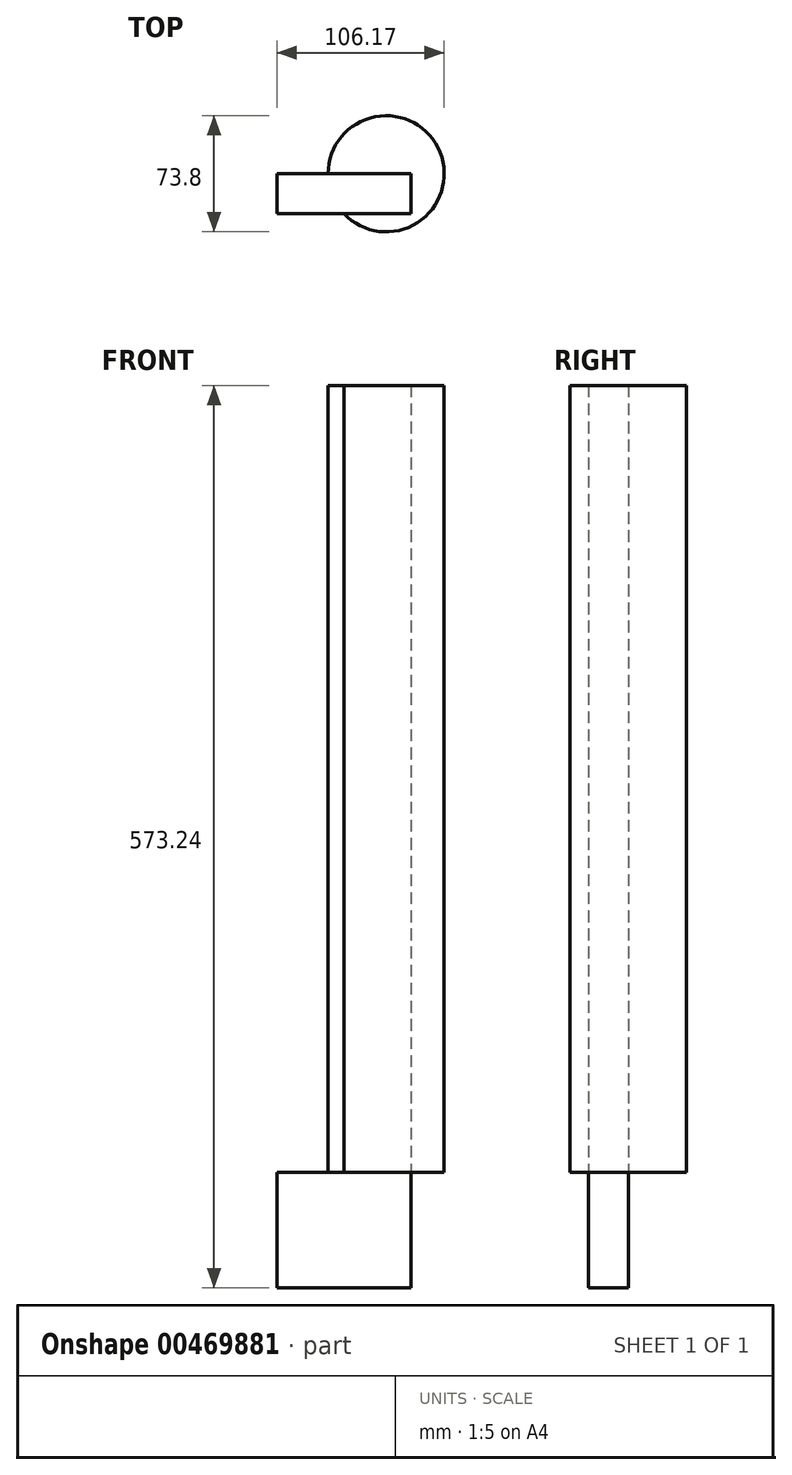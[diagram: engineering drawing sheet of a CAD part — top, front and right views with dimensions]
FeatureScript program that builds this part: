
annotation { "Feature Type Name" : "Feature", "Feature Type Description" : "" }
export const myFeature = defineFeature(function(context is Context, id is Id, definition is map)
    precondition{}
    {
        {
            var Q0;
            Q0=qCreatedBy(makeId("Front.planeOp"),FACE);
            var sketch = newSketch(context, id + "F0", { "sketchPlane" : qUnion([Q0])});
            skLineSegment(sketch, "E0.bottom", {"start": v(85.15, 0) * mm, "end": v(0, 0) * mm});
            skLineSegment(sketch, "E0.top", {"start": v(85.15, 73.24) * mm, "end": v(0, 73.24) * mm});
            skLineSegment(sketch, "E0.left", {"start": v(85.15, 0) * mm, "end": v(85.15, 73.24) * mm});
            skLineSegment(sketch, "E0.right", {"start": v(0, 0) * mm, "end": v(0, 73.24) * mm});
            skSolve(sketch);
        }
        {
            var Q0;
            Q0=makeQuery(id+"F0.imprint","IMPRINT",FACE,{"disambiguationData":[TD([[makeQuery(id+"F0.imprint","IMPRINT",EDGE,{"derivedFrom":sQuery(id+"F0.wireOp",EDGE,"E0.bottom")}),-1.0]])]});
            extrude(context, id + "F1", {"entities" : qUnion([Q0]), "depth" : 25.4 * mm});
        }
        {
            var Q0;
            Q0=makeQuery(id+"F1.opExtrude","SWEPT_FACE",FACE,{"disambiguationData":[OSD([sQuery(id+"F0.wireOp",EDGE,"E0.top")])]});
            var sketch = newSketch(context, id + "F2", { "sketchPlane" : qUnion([Q0])});
            skCircle(sketch, "E1", {"center": v(69.28, 0) * mm, "radius": 36.9 * mm});
            skSolve(sketch);
        }
        {
            var Q0;
            {var subQ1=sQuery(id+"F0.wireOp",EDGE,"E0.top");var subQ6=makeQuery(id+"F1.opExtrude","SWEPT_EDGE",EDGE,{"disambiguationData":[OSD([subQ1,sQuery(id+"F0.wireOp",EDGE,"E0.left")])]});Q0=makeQuery(id+"F2.imprint","IMPRINT",FACE,{"disambiguationData":[TD([[makeQuery(id+"F2.imprint","IMPRINT",EDGE,{"derivedFrom":subQ6}),-1.0]])]});}
            extrude(context, id + "F3", {"entities" : qUnion([Q0]), "depth" : 500 * mm});
        }
    });
